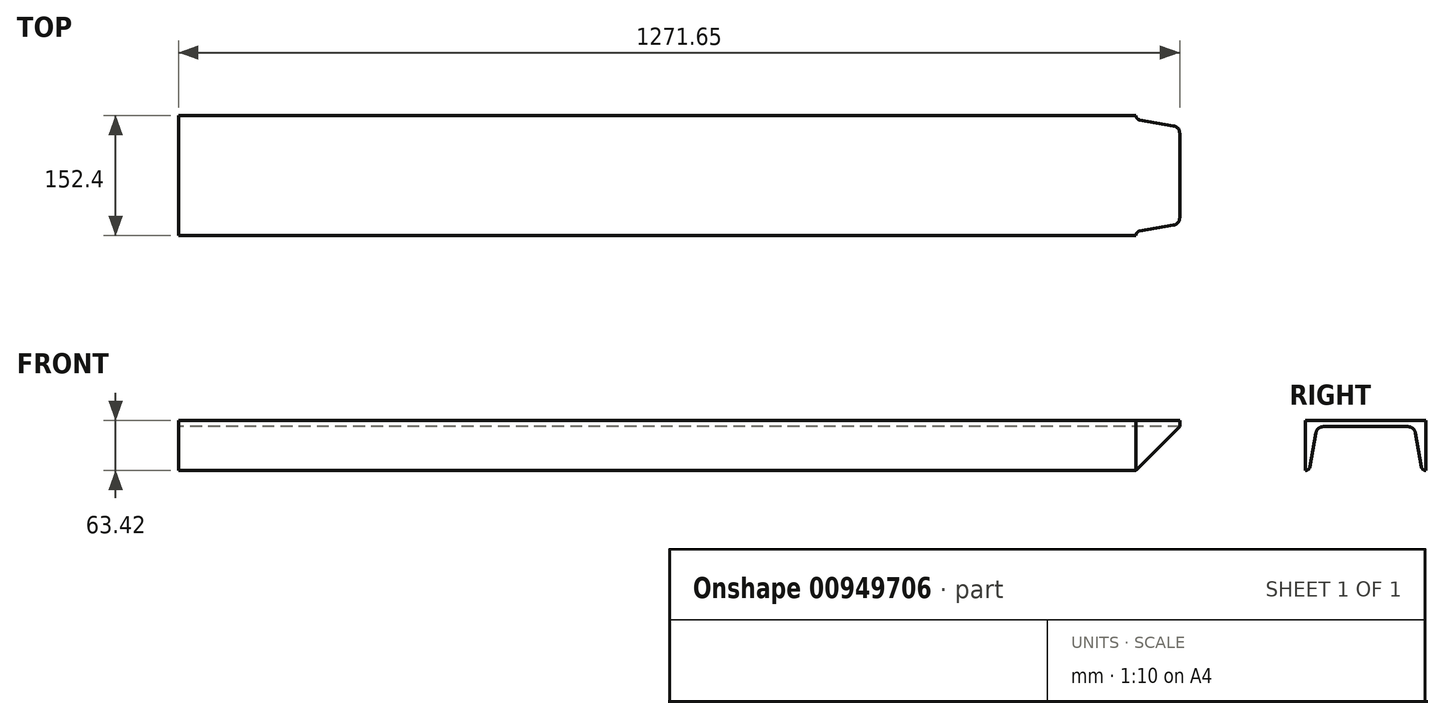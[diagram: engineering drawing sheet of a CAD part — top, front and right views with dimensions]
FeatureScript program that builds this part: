
annotation { "Feature Type Name" : "Feature", "Feature Type Description" : "" }
export const myFeature = defineFeature(function(context is Context, id is Id, definition is map)
    precondition{}
    {
        {
            var Q0;
            Q0=qCreatedBy(makeId("Right.planeOp"),FACE);
            var sketch = newSketch(context, id + "F0", { "sketchPlane" : qUnion([Q0])});
            skLineSegment(sketch, "E0", {"start": v(-76.2, 0) * mm, "end": v(76.2, 0) * mm});
            skLineSegment(sketch, "E1", {"start": v(76.2, 0) * mm, "end": v(76.2, -63.42) * mm});
            skLineSegment(sketch, "E2", {"start": v(-76.2, 0) * mm, "end": v(-76.2, -63.42) * mm});
            skLineSegment(sketch, "E3", {"start": v(-63.12, -15.57) * mm, "end": v(-70.65, -58.76) * mm});
            skLineSegment(sketch, "E4", {"start": v(63.12, -15.57) * mm, "end": v(70.65, -58.76) * mm});
            skLineSegment(sketch, "E5", {"start": v(-53.98, -7.87) * mm, "end": v(53.98, -7.87) * mm});
            skArc(sketch, "E6.filletArc", {"start": v(-76.2, -63.42) * mm, "mid": v(-72.57, -62.1) * mm, "end": v(-70.65, -58.76) * mm});
            skArc(sketch, "E7.filletArc", {"start": v(70.65, -58.76) * mm, "mid": v(72.57, -62.1) * mm, "end": v(76.2, -63.42) * mm});
            skArc(sketch, "E8.filletArc", {"start": v(-53.98, -7.87) * mm, "mid": v(-59.95, -10.05) * mm, "end": v(-63.12, -15.57) * mm});
            skArc(sketch, "E9.filletArc", {"start": v(63.12, -15.57) * mm, "mid": v(59.95, -10.05) * mm, "end": v(53.98, -7.87) * mm});
            skSolve(sketch);
        }
        {
            var Q0;
            Q0=qSketchRegion(id+"F0",true);
            extrude(context, id + "F1", {"entities" : qUnion([Q0]), "depth" : 1279.52 * mm, "offsetDistance" : 25.4 * mm});
        }
        {
            var Q0;
            Q0=makeQuery(id+"F1.opExtrude","SWEPT_FACE",FACE,{"disambiguationData":[OSD([sQuery(id+"F0.wireOp",EDGE,"E0")])]});
            var sketch = newSketch(context, id + "F2", { "sketchPlane" : qUnion([Q0])});
            skLineSegment(sketch, "E10", {"start": v(1279.53, 76.2) * mm, "end": v(1279.53, -76.2) * mm});
            skLineSegment(sketch, "E11", {"start": v(1279.53, -76.2) * mm, "end": v(1216.1, -76.2) * mm});
            skLineSegment(sketch, "E12", {"start": v(1279.53, 76.2) * mm, "end": v(1216.1, 76.2) * mm});
            skLineSegment(sketch, "E13", {"start": v(1263.96, 63.12) * mm, "end": v(1220.77, 70.65) * mm});
            skLineSegment(sketch, "E14", {"start": v(1263.96, -63.12) * mm, "end": v(1220.77, -70.65) * mm});
            skLineSegment(sketch, "E15", {"start": v(1271.65, 53.98) * mm, "end": v(1271.65, -53.98) * mm});
            skArc(sketch, "E16.filletArc", {"start": v(1216.1, 76.2) * mm, "mid": v(1217.42, 72.57) * mm, "end": v(1220.77, 70.65) * mm});
            skArc(sketch, "E17.filletArc", {"start": v(1220.77, -70.65) * mm, "mid": v(1217.42, -72.57) * mm, "end": v(1216.1, -76.2) * mm});
            skArc(sketch, "E18.filletArc", {"start": v(1271.65, 53.98) * mm, "mid": v(1269.47, 59.95) * mm, "end": v(1263.96, 63.12) * mm});
            skArc(sketch, "E19.filletArc", {"start": v(1263.96, -63.12) * mm, "mid": v(1269.47, -59.95) * mm, "end": v(1271.65, -53.98) * mm});
            skSolve(sketch);
        }
        {
            var Q0;
            Q0 = qSketchRegion(id + "F2", true);
            extrude(context, id + "F3", {"entities" : qUnion([Q0]), "operationType" : NewBodyOperationType.REMOVE, "endBound" : BoundingType.THROUGH_ALL, "oppositeDirection" : true, "depth" : 25.4 * mm, "offsetDistance" : 25.4 * mm});
        }
    });
